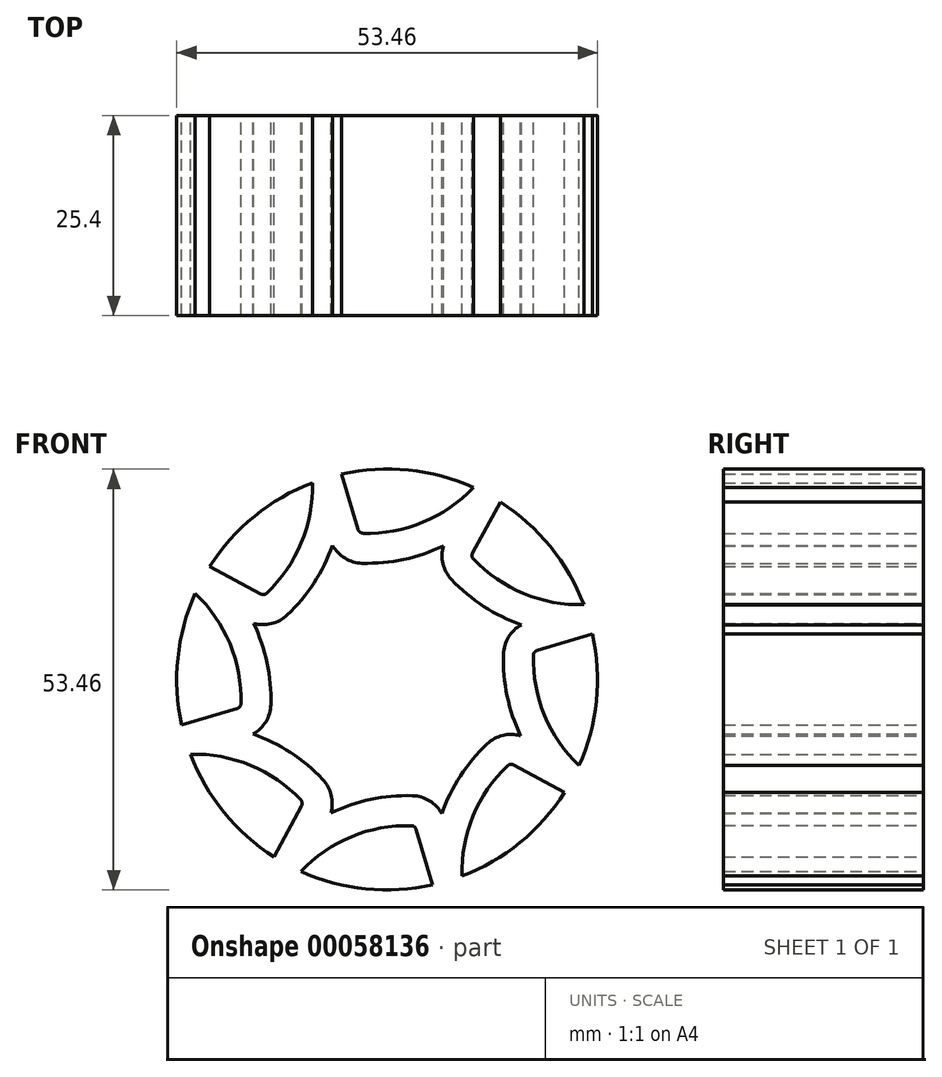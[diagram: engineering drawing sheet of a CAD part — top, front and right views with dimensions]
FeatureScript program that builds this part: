
annotation { "Feature Type Name" : "Feature", "Feature Type Description" : "" }
export const myFeature = defineFeature(function(context is Context, id is Id, definition is map)
    precondition{}
    {
        {
            var Q0;
            Q0=qCreatedBy(makeId("Front.planeOp"),FACE);
            var sketch = newSketch(context, id + "F0", { "sketchPlane" : qUnion([Q0])});
            skLineSegment(sketch, "E0", {"start": v(0, 0) * mm, "end": v(7.45, 13.75) * mm, "construction": true});
            skArc(sketch, "E1", {"start": v(-9.43, 25) * mm, "mid": v(-16.84, 20.75) * mm, "end": v(-22.54, 14.37) * mm});
            skLineSegment(sketch, "E2", {"start": v(-35.5, 7.62) * mm, "end": v(72.22, 7.62) * mm, "construction": true});
            skPoint(sketch, "E3", {"position": v(25.62, 7.62) * mm});
            skLineSegment(sketch, "E4", {"start": v(0, 0) * mm, "end": v(25.62, 7.62) * mm, "construction": true});
            skArc(sketch, "E5", {"start": v(23.3, 7.62) * mm, "mid": v(24.46, 7.59) * mm, "end": v(25.62, 7.62) * mm});
            skPoint(sketch, "E6.visualSharp", {"position": v(8.35, 15.42) * mm});
            skLineSegment(sketch, "E7.0.left", {"start": v(14.4, 22.6) * mm, "end": v(10.86, 16.05) * mm});
            skLineSegment(sketch, "E7.0.right", {"start": v(11.05, 24.4) * mm, "end": v(11.02, 24.35) * mm});
            skArc(sketch, "E7.1.left", {"start": v(10.86, 16.05) * mm, "mid": v(10.79, 15.67) * mm, "end": v(10.95, 15.31) * mm});
            skArc(sketch, "E7.1.right", {"start": v(7.14, 16.96) * mm, "mid": v(7.1, 14.7) * mm, "end": v(8.18, 12.7) * mm});
            skArc(sketch, "E7.2.endCap", {"start": v(26.1, 5.78) * mm, "mid": v(25.91, 5.74) * mm, "end": v(25.72, 5.72) * mm});
            skArc(sketch, "E7.2.left", {"start": v(10.95, 15.31) * mm, "mid": v(17.35, 10.9) * mm, "end": v(24.98, 9.5) * mm});
            skArc(sketch, "E7.2.right", {"start": v(8.18, 12.7) * mm, "mid": v(12.27, 9.3) * mm, "end": v(17.04, 6.95) * mm});
            skLineSegment(sketch, "E8.trimOffspring", {"start": v(8.35, 15.42) * mm, "end": v(30.97, 57.2) * mm, "construction": true});
            skLineSegment(sketch, "E9.1.0", {"start": v(-9.45, 25.07) * mm, "end": v(-9.43, 25) * mm});
            skLineSegment(sketch, "E9.1.1", {"start": v(-5.8, 26.16) * mm, "end": v(-3.67, 19.03) * mm});
            skArc(sketch, "E9.1.2", {"start": v(-6.95, 17.04) * mm, "mid": v(-5.37, 15.4) * mm, "end": v(-3.2, 14.77) * mm});
            skArc(sketch, "E9.1.3", {"start": v(-3.2, 14.77) * mm, "mid": v(2.1, 15.25) * mm, "end": v(7.14, 16.96) * mm});
            skArc(sketch, "E9.1.4", {"start": v(-3.08, 18.57) * mm, "mid": v(4.55, 19.98) * mm, "end": v(10.95, 24.38) * mm});
            skArc(sketch, "E9.1.5", {"start": v(14.37, 22.54) * mm, "mid": v(14.26, 22.38) * mm, "end": v(14.15, 22.23) * mm});
            skArc(sketch, "E9.1.6", {"start": v(-3.67, 19.03) * mm, "mid": v(-3.45, 18.7) * mm, "end": v(-3.08, 18.57) * mm});
            skLineSegment(sketch, "E9.2.0", {"start": v(-24.4, 11.05) * mm, "end": v(-24.35, 11.02) * mm});
            skLineSegment(sketch, "E9.2.1", {"start": v(-22.6, 14.4) * mm, "end": v(-16.05, 10.86) * mm});
            skArc(sketch, "E9.2.2", {"start": v(-16.96, 7.14) * mm, "mid": v(-14.7, 7.1) * mm, "end": v(-12.7, 8.18) * mm});
            skArc(sketch, "E9.2.3", {"start": v(-12.7, 8.18) * mm, "mid": v(-9.3, 12.27) * mm, "end": v(-6.95, 17.04) * mm});
            skArc(sketch, "E9.2.4", {"start": v(-15.31, 10.95) * mm, "mid": v(-10.9, 17.35) * mm, "end": v(-9.5, 24.98) * mm});
            skArc(sketch, "E9.2.5", {"start": v(-5.78, 26.1) * mm, "mid": v(-5.74, 25.91) * mm, "end": v(-5.72, 25.72) * mm});
            skArc(sketch, "E9.2.6", {"start": v(-16.05, 10.86) * mm, "mid": v(-15.67, 10.79) * mm, "end": v(-15.31, 10.95) * mm});
            skLineSegment(sketch, "E9.3.0", {"start": v(-25.07, -9.45) * mm, "end": v(-25, -9.43) * mm});
            skLineSegment(sketch, "E9.3.1", {"start": v(-26.16, -5.8) * mm, "end": v(-19.03, -3.67) * mm});
            skArc(sketch, "E9.3.2", {"start": v(-17.04, -6.95) * mm, "mid": v(-15.4, -5.37) * mm, "end": v(-14.77, -3.2) * mm});
            skArc(sketch, "E9.3.3", {"start": v(-14.77, -3.2) * mm, "mid": v(-15.25, 2.1) * mm, "end": v(-16.96, 7.14) * mm});
            skArc(sketch, "E9.3.4", {"start": v(-18.57, -3.08) * mm, "mid": v(-19.98, 4.55) * mm, "end": v(-24.38, 10.95) * mm});
            skArc(sketch, "E9.3.5", {"start": v(-22.54, 14.37) * mm, "mid": v(-22.38, 14.26) * mm, "end": v(-22.23, 14.15) * mm});
            skArc(sketch, "E9.3.6", {"start": v(-19.03, -3.67) * mm, "mid": v(-18.7, -3.45) * mm, "end": v(-18.57, -3.08) * mm});
            skLineSegment(sketch, "E9.4.0", {"start": v(-11.05, -24.4) * mm, "end": v(-11.02, -24.35) * mm});
            skLineSegment(sketch, "E9.4.1", {"start": v(-14.4, -22.6) * mm, "end": v(-10.86, -16.05) * mm});
            skArc(sketch, "E9.4.2", {"start": v(-7.14, -16.96) * mm, "mid": v(-7.1, -14.7) * mm, "end": v(-8.18, -12.7) * mm});
            skArc(sketch, "E9.4.3", {"start": v(-8.18, -12.7) * mm, "mid": v(-12.27, -9.3) * mm, "end": v(-17.04, -6.95) * mm});
            skArc(sketch, "E9.4.4", {"start": v(-10.95, -15.31) * mm, "mid": v(-17.35, -10.9) * mm, "end": v(-24.98, -9.5) * mm});
            skArc(sketch, "E9.4.5", {"start": v(-26.1, -5.78) * mm, "mid": v(-25.91, -5.74) * mm, "end": v(-25.72, -5.72) * mm});
            skArc(sketch, "E9.4.6", {"start": v(-10.86, -16.05) * mm, "mid": v(-10.79, -15.67) * mm, "end": v(-10.95, -15.31) * mm});
            skLineSegment(sketch, "E9.5.0", {"start": v(9.45, -25.07) * mm, "end": v(9.43, -25) * mm});
            skLineSegment(sketch, "E9.5.1", {"start": v(5.8, -26.16) * mm, "end": v(3.67, -19.03) * mm});
            skArc(sketch, "E9.5.2", {"start": v(6.95, -17.04) * mm, "mid": v(5.37, -15.4) * mm, "end": v(3.2, -14.77) * mm});
            skArc(sketch, "E9.5.3", {"start": v(3.2, -14.77) * mm, "mid": v(-2.1, -15.25) * mm, "end": v(-7.14, -16.96) * mm});
            skArc(sketch, "E9.5.4", {"start": v(3.08, -18.57) * mm, "mid": v(-4.55, -19.98) * mm, "end": v(-10.95, -24.38) * mm});
            skArc(sketch, "E9.5.5", {"start": v(-14.37, -22.54) * mm, "mid": v(-14.26, -22.38) * mm, "end": v(-14.15, -22.23) * mm});
            skArc(sketch, "E9.5.6", {"start": v(3.67, -19.03) * mm, "mid": v(3.45, -18.7) * mm, "end": v(3.08, -18.57) * mm});
            skLineSegment(sketch, "E9.6.0", {"start": v(24.4, -11.05) * mm, "end": v(24.35, -11.02) * mm});
            skLineSegment(sketch, "E9.6.1", {"start": v(22.6, -14.4) * mm, "end": v(16.05, -10.86) * mm});
            skArc(sketch, "E9.6.2", {"start": v(16.96, -7.14) * mm, "mid": v(14.7, -7.1) * mm, "end": v(12.7, -8.18) * mm});
            skArc(sketch, "E9.6.3", {"start": v(12.7, -8.18) * mm, "mid": v(9.3, -12.27) * mm, "end": v(6.95, -17.04) * mm});
            skArc(sketch, "E9.6.4", {"start": v(15.31, -10.95) * mm, "mid": v(10.9, -17.35) * mm, "end": v(9.5, -24.98) * mm});
            skArc(sketch, "E9.6.5", {"start": v(5.78, -26.1) * mm, "mid": v(5.74, -25.91) * mm, "end": v(5.72, -25.72) * mm});
            skArc(sketch, "E9.6.6", {"start": v(16.05, -10.86) * mm, "mid": v(15.67, -10.79) * mm, "end": v(15.31, -10.95) * mm});
            skLineSegment(sketch, "E9.7.0", {"start": v(25.07, 9.45) * mm, "end": v(25, 9.43) * mm});
            skLineSegment(sketch, "E9.7.1", {"start": v(26.16, 5.8) * mm, "end": v(19.03, 3.67) * mm});
            skArc(sketch, "E9.7.2", {"start": v(17.04, 6.95) * mm, "mid": v(15.4, 5.37) * mm, "end": v(14.77, 3.2) * mm});
            skArc(sketch, "E9.7.3", {"start": v(14.77, 3.2) * mm, "mid": v(15.25, -2.1) * mm, "end": v(16.96, -7.14) * mm});
            skArc(sketch, "E9.7.4", {"start": v(18.57, 3.08) * mm, "mid": v(19.98, -4.55) * mm, "end": v(24.38, -10.95) * mm});
            skArc(sketch, "E9.7.5", {"start": v(22.54, -14.37) * mm, "mid": v(22.38, -14.26) * mm, "end": v(22.23, -14.15) * mm});
            skArc(sketch, "E9.7.6", {"start": v(19.03, 3.67) * mm, "mid": v(18.7, 3.45) * mm, "end": v(18.57, 3.08) * mm});
            skPoint(sketch, "E10.orphan", {"position": v(-7.32, 17.94) * mm});
            skPoint(sketch, "E11.orphan", {"position": v(7.5, 17.87) * mm});
            skPoint(sketch, "E12.orphan", {"position": v(17.94, 7.32) * mm});
            skPoint(sketch, "E13.orphan", {"position": v(17.87, -7.5) * mm});
            skPoint(sketch, "E14.orphan", {"position": v(7.32, -17.94) * mm});
            skPoint(sketch, "E15.orphan", {"position": v(-7.5, -17.87) * mm});
            skPoint(sketch, "E16.orphan", {"position": v(-17.94, -7.32) * mm});
            skLineSegment(sketch, "E17.trimOffspring", {"start": v(-18.07, 7.62) * mm, "end": v(-17.87, 7.5) * mm});
            skPoint(sketch, "E18.orphan", {"position": v(-17.87, 7.5) * mm});
            skArc(sketch, "E19.trimOffspring", {"start": v(11.02, 24.35) * mm, "mid": v(2.76, 26.58) * mm, "end": v(-5.78, 26.1) * mm});
            skArc(sketch, "E20.trimOffspring", {"start": v(-24.35, 11.02) * mm, "mid": v(-26.58, 2.76) * mm, "end": v(-26.1, -5.78) * mm});
            skArc(sketch, "E21.trimOffspring", {"start": v(25, 9.43) * mm, "mid": v(20.75, 16.84) * mm, "end": v(14.37, 22.54) * mm});
            skArc(sketch, "E22.trimOffspring", {"start": v(24.35, -11.02) * mm, "mid": v(26.58, -2.76) * mm, "end": v(26.1, 5.78) * mm});
            skArc(sketch, "E23.trimOffspring", {"start": v(9.43, -25) * mm, "mid": v(16.84, -20.75) * mm, "end": v(22.54, -14.37) * mm});
            skArc(sketch, "E24.trimOffspring", {"start": v(-11.02, -24.35) * mm, "mid": v(-2.76, -26.58) * mm, "end": v(5.78, -26.1) * mm});
            skArc(sketch, "E25.trimOffspring", {"start": v(-25, -9.43) * mm, "mid": v(-20.75, -16.84) * mm, "end": v(-14.37, -22.54) * mm});
            skSolve(sketch);
        }
        {
            var Q0;
            Q0 = qSketchRegion(id + "F0", true);
            extrude(context, id + "F1", {"entities" : qUnion([Q0]), "depth" : 25.4 * mm});
        }
    });
